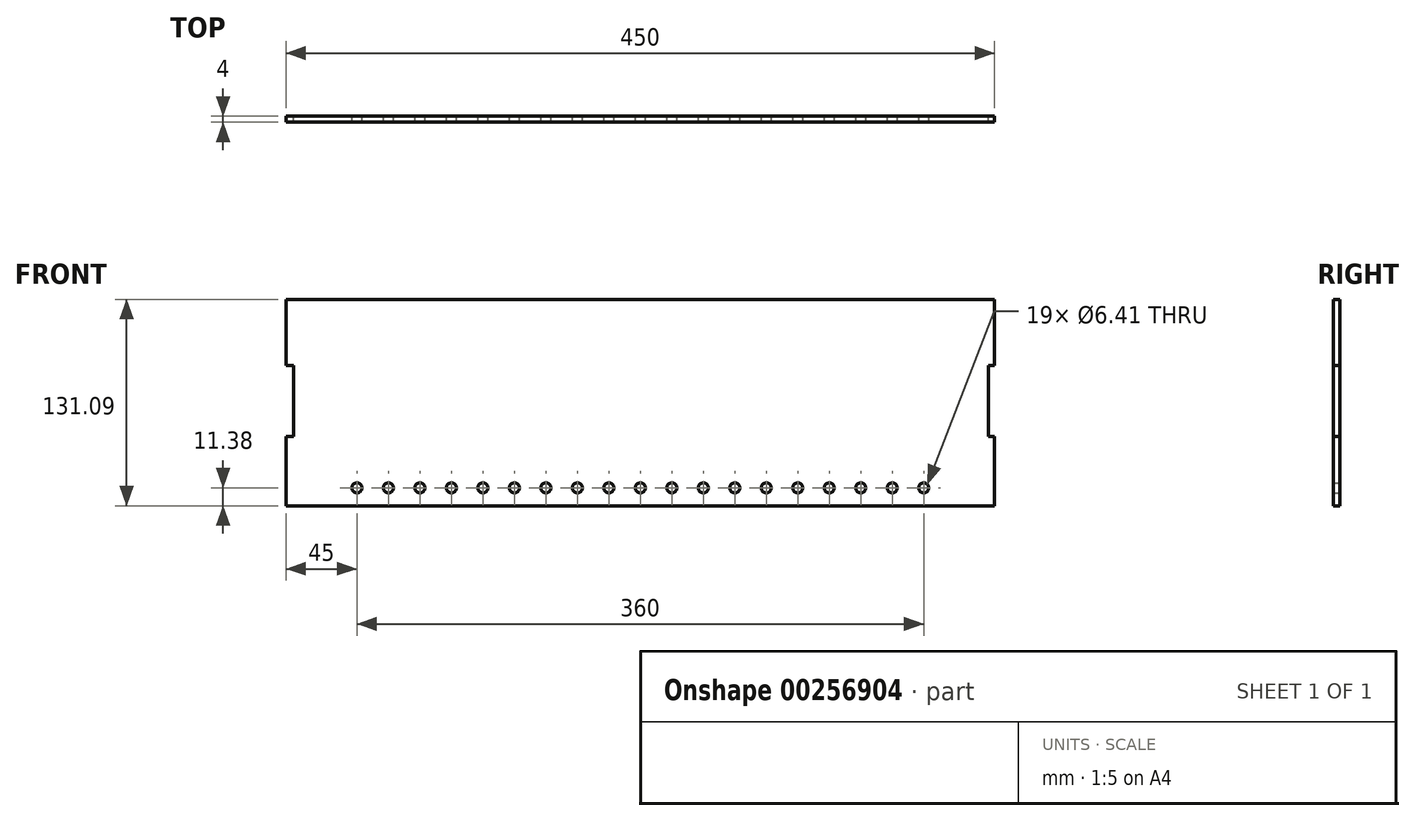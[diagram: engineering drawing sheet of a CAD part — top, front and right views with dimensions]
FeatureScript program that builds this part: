
annotation { "Feature Type Name" : "Feature", "Feature Type Description" : "" }
export const myFeature = defineFeature(function(context is Context, id is Id, definition is map)
    precondition{}
    {
        {
            var Q0;
            Q0=qCreatedBy(makeId("Front.planeOp"),FACE);
            var sketch = newSketch(context, id + "F0", { "sketchPlane" : qUnion([Q0])});
            skLineSegment(sketch, "E0.bottom", {"start": v(0, 0) * mm, "end": v(450, 0) * mm});
            skLineSegment(sketch, "E0.top", {"start": v(0, 131.1) * mm, "end": v(450, 131.1) * mm});
            skLineSegment(sketch, "E0.left", {"start": v(0, 0) * mm, "end": v(0, 44) * mm});
            skLineSegment(sketch, "E0.right", {"start": v(450, 0) * mm, "end": v(450, 44) * mm});
            skLineSegment(sketch, "E1.bottom", {"start": v(0, 44) * mm, "end": v(4.85, 44) * mm});
            skLineSegment(sketch, "E1.top", {"start": v(0, 89) * mm, "end": v(4.85, 89) * mm});
            skLineSegment(sketch, "E1.right", {"start": v(4.85, 44) * mm, "end": v(4.85, 89) * mm});
            skLineSegment(sketch, "E2", {"start": v(0, 89) * mm, "end": v(0, 131.1) * mm});
            skLineSegment(sketch, "E3.bottom", {"start": v(450, 89) * mm, "end": v(446, 89) * mm});
            skLineSegment(sketch, "E3.top", {"start": v(450, 44) * mm, "end": v(446, 44) * mm});
            skLineSegment(sketch, "E3.right", {"start": v(446, 89) * mm, "end": v(446, 44) * mm});
            skLineSegment(sketch, "E4.trimOffspring", {"start": v(450, 89) * mm, "end": v(450, 131.1) * mm});
            skCircle(sketch, "E5", {"center": v(225, 11.38) * mm, "radius": 3.2 * mm});
            skPoint(sketch, "E5.centerSnap0", {"position": v(225, 0) * mm});
            skCircle(sketch, "E6.1.0.0", {"center": v(245, 11.38) * mm, "radius": 3.2 * mm});
            skCircle(sketch, "E6.2.0.0", {"center": v(265, 11.38) * mm, "radius": 3.2 * mm});
            skCircle(sketch, "E6.3.0.0", {"center": v(285, 11.38) * mm, "radius": 3.2 * mm});
            skCircle(sketch, "E6.4.0.0", {"center": v(305, 11.38) * mm, "radius": 3.2 * mm});
            skCircle(sketch, "E6.5.0.0", {"center": v(325, 11.38) * mm, "radius": 3.2 * mm});
            skCircle(sketch, "E6.6.0.0", {"center": v(345, 11.38) * mm, "radius": 3.2 * mm});
            skCircle(sketch, "E6.7.0.0", {"center": v(365, 11.38) * mm, "radius": 3.2 * mm});
            skCircle(sketch, "E6.8.0.0", {"center": v(385, 11.38) * mm, "radius": 3.2 * mm});
            skCircle(sketch, "E6.9.0.0", {"center": v(405, 11.38) * mm, "radius": 3.2 * mm});
            skLineSegment(sketch, "E6.direction1", {"start": v(225, 11.38) * mm, "end": v(245, 11.38) * mm, "construction": true});
            skCircle(sketch, "E7.1.0.0", {"center": v(205, 11.38) * mm, "radius": 3.2 * mm});
            skCircle(sketch, "E7.2.0.0", {"center": v(185, 11.38) * mm, "radius": 3.2 * mm});
            skCircle(sketch, "E7.3.0.0", {"center": v(165, 11.38) * mm, "radius": 3.2 * mm});
            skCircle(sketch, "E7.4.0.0", {"center": v(145, 11.38) * mm, "radius": 3.2 * mm});
            skCircle(sketch, "E7.5.0.0", {"center": v(125, 11.38) * mm, "radius": 3.2 * mm});
            skCircle(sketch, "E7.6.0.0", {"center": v(105, 11.38) * mm, "radius": 3.2 * mm});
            skCircle(sketch, "E7.7.0.0", {"center": v(85, 11.38) * mm, "radius": 3.2 * mm});
            skCircle(sketch, "E7.8.0.0", {"center": v(65, 11.38) * mm, "radius": 3.2 * mm});
            skCircle(sketch, "E7.9.0.0", {"center": v(45, 11.38) * mm, "radius": 3.2 * mm});
            skLineSegment(sketch, "E7.direction1", {"start": v(225, 11.38) * mm, "end": v(205, 11.38) * mm, "construction": true});
            skSolve(sketch);
        }
        {
            var Q0;
            Q0=makeQuery(id+"F0.imprint","IMPRINT",FACE,{"disambiguationData":[TD([[makeQuery(id+"F0.imprint","IMPRINT",EDGE,{"derivedFrom":sQuery(id+"F0.wireOp",EDGE,"E0.bottom")}),1.0]])]});
            extrude(context, id + "F1", {"entities" : qUnion([Q0]), "depth" : 4 * mm});
        }
    });
